# Revit family: Exhaust_Fan-BroanNutone-Ultra_Green-XB110
name_source: partatom
category: Mechanical Equipment
units: mm (PartAtom-declared; Revit-internal decimal feet)

## family parameters
Cut with Voids When Loaded = No
Host = Face
OmniClass Number = 23.75.35.17.17
OmniClass Title = Room Air Circulation Fans
Part Type = Normal
Room Calculation Point = No
Round Connector Dimension = Use Radius
Shared = No

## types (1)
- XB110
    Air Volume = 110 CFM
    Assembly Code = E1090900
    Cover Finish = Plastic - Broan NuTone - White
    Default Elevation = 4' - 0"
    Description = Ceiling Bathroom Exhaust Fan, ENERGY STAR®
    Electrical Connector = Electrical Connection
    Exhaust Connector = Exhaust Connection
    Exhaust Diameter = 0' - 6"
    Exhaust Radius = 0' - 3"
    Fan Body Finish = Metal - Broan NuTone - Steel
    Fan Wattage = 8 W
    Frequency = 60 Hz
    Height = 6' - 5 5/8"
    Housing Height = 0' - 7 5/8"
    Housing Length = 0' - 10 1/32"
    Housing Width = 0' - 11 3/8"
    Length = 1' - 1"
    Manufacturer = Broan
    Model = XB110
    Noise = 1.2
    Number of Poles = 1
    Phase = 1
    Power Factor = 1
    Product Documentation Link = https://www.broan-nutone.com
    Product Name = ULTRA GREEN XB Series 110 CFM Ceiling Bathroom Exhaust Fan, ENERGY STAR®
    Product Page URL = https://www.broan-nutone.com
    URL = https://www.broan-nutone.com
    Voltage = 120 V
    Width = 1' - 1 3/4"

## geometry (parser evidence)
native form markers: Sweep x1
no freeform markers — native parametric forms only
